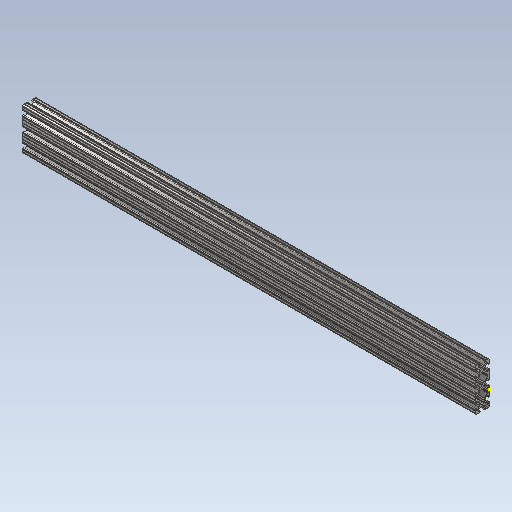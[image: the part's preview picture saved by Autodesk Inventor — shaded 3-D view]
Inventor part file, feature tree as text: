
AUTODESK INVENTOR PART (.ipt)
format: ipt  version: 2020 (Build 240168000, 168)  size: 407,040 bytes
history: native  units: in
note: dims shown in document units (in); Inventor stores cm internally (conversion verified against a paired STEP export)
features: sketch x2, extrude x1
ambient origin geometry x8: Origin, YZ Plane, XZ Plane, XY Plane, X Axis, Y Axis, Z Axis, Center Point
bodies: Solid1 (feature_tree)
feature tree (3):
  extrude  "Extrusion1"  [1 undecoded]
  sketch  "Sketch2"
  sketch  "Sketch1"  dims[d0=32.0in d1=0.0in]
note: 1 required parameter value undecoded (feature->parameter linkage not recoverable at this tier; creation-order binding heuristic only, values carry confidence <= 0.55)
